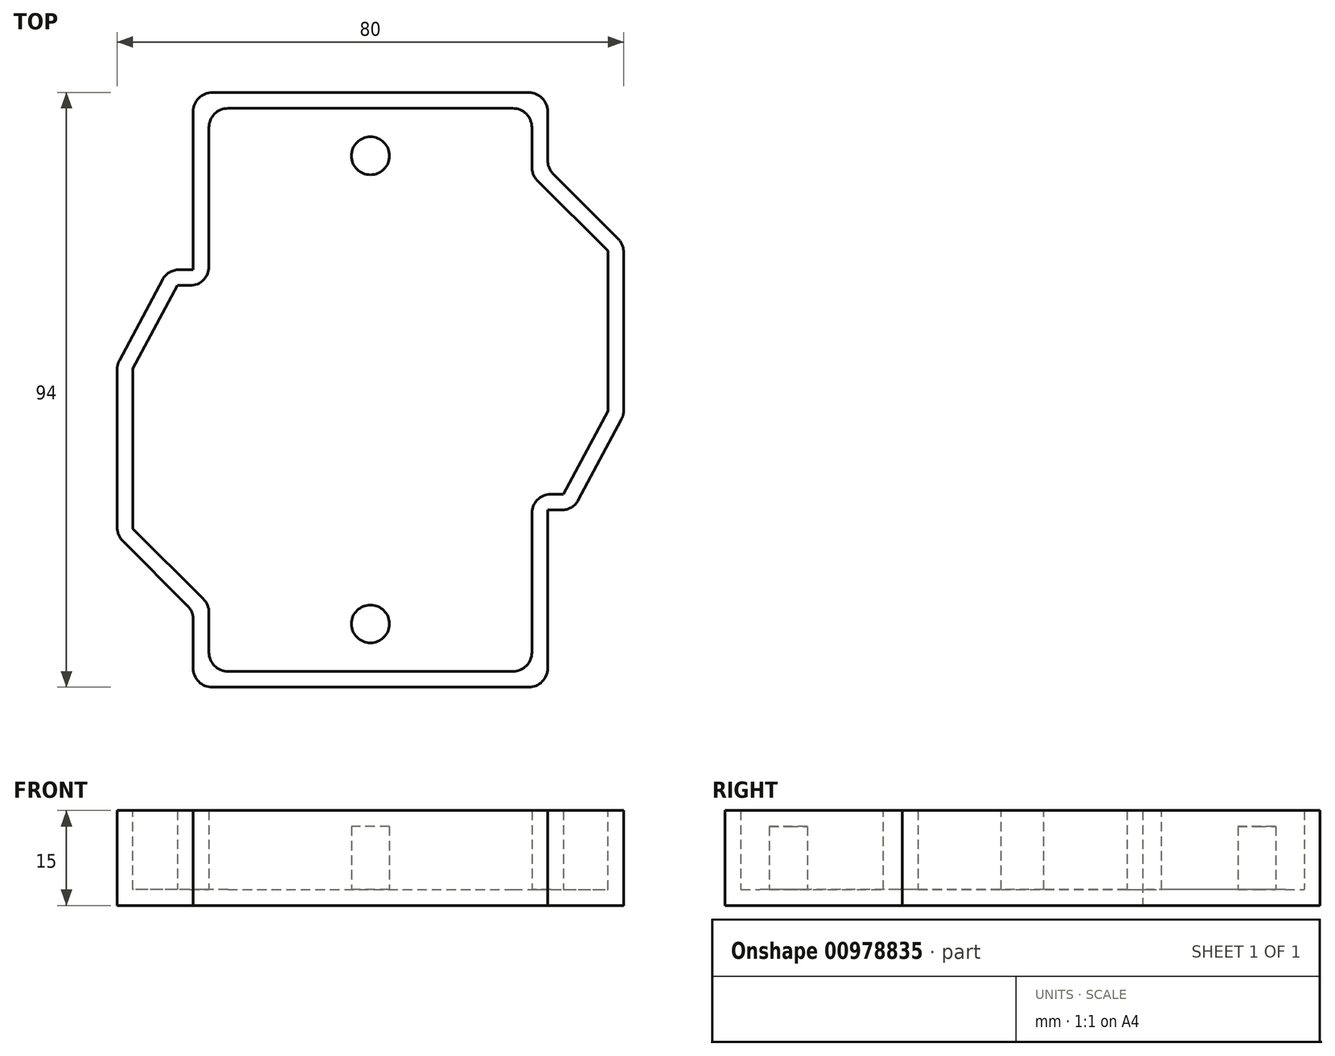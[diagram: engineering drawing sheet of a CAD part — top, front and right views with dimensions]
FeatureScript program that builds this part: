
annotation { "Feature Type Name" : "Feature", "Feature Type Description" : "" }
export const myFeature = defineFeature(function(context is Context, id is Id, definition is map)
    precondition{}
    {
        {
            var Q0;
            Q0=qCreatedBy(makeId("Top.planeOp"),FACE);
            var sketch = newSketch(context, id + "F0", { "sketchPlane" : qUnion([Q0])});
            skLineSegment(sketch, "E0.bottom", {"start": v(-72.44, 119.95) * mm, "end": v(-16.44, 119.95) * mm});
            skLineSegment(sketch, "E0.top", {"start": v(-72.44, 25.95) * mm, "end": v(-16.44, 25.95) * mm});
            skLineSegment(sketch, "E0.left", {"start": v(-72.44, 119.95) * mm, "end": v(-72.44, 25.95) * mm});
            skLineSegment(sketch, "E0.right", {"start": v(-16.44, 119.95) * mm, "end": v(-16.44, 25.95) * mm});
            skLineSegment(sketch, "E1.bottom", {"start": v(-72.44, 91.95) * mm, "end": v(-84.44, 91.95) * mm});
            skLineSegment(sketch, "E1.top", {"start": v(-72.44, 37.95) * mm, "end": v(-84.44, 37.95) * mm});
            skLineSegment(sketch, "E1.left", {"start": v(-72.44, 91.95) * mm, "end": v(-72.44, 37.95) * mm});
            skLineSegment(sketch, "E1.right", {"start": v(-84.44, 91.95) * mm, "end": v(-84.44, 37.95) * mm});
            skLineSegment(sketch, "E2.bottom", {"start": v(-16.44, 53.95) * mm, "end": v(-4.44, 53.95) * mm});
            skLineSegment(sketch, "E2.top", {"start": v(-16.44, 107.95) * mm, "end": v(-4.44, 107.95) * mm});
            skLineSegment(sketch, "E2.left", {"start": v(-16.44, 53.95) * mm, "end": v(-16.44, 107.95) * mm});
            skLineSegment(sketch, "E2.right", {"start": v(-4.44, 53.95) * mm, "end": v(-4.44, 107.95) * mm});
            skSolve(sketch);
        }
        {
            var Q0;
            Q0 = qSketchRegion(id + "F0", true);
            extrude(context, id + "F1", {"entities" : qUnion([Q0]), "depth" : 15 * mm, "offsetDistance" : 25 * mm});
        }
        {
            var Q0;
            Q0=makeQuery(id+"F1.opExtrude","SWEPT_EDGE",EDGE,{"disambiguationData":[OSD([sQuery(id+"F0.wireOp",EDGE,"E1.bottom"),sQuery(id+"F0.wireOp",EDGE,"E1.right")])]});
            var Q1;
            Q1=makeQuery(id+"F1.opExtrude","SWEPT_EDGE",EDGE,{"disambiguationData":[OSD([sQuery(id+"F0.wireOp",EDGE,"E2.bottom"),sQuery(id+"F0.wireOp",EDGE,"E2.right")])]});
            chamfer(context, id + "F2", {"entities" : qUnion([Q0, Q1]), "chamferType" : ChamferType.TWO_OFFSETS, "width1" : 15 * mm, "oppositeDirection" : false, "width2" : 8 * mm, "tangentPropagation" : true});
        }
        {
            var Q0;
            Q0=makeQuery(id+"F1.opExtrude","SWEPT_EDGE",EDGE,{"disambiguationData":[OSD([sQuery(id+"F0.wireOp",EDGE,"E1.top"),sQuery(id+"F0.wireOp",EDGE,"E1.right")])]});
            var Q1;
            Q1=makeQuery(id+"F1.opExtrude","SWEPT_EDGE",EDGE,{"disambiguationData":[OSD([sQuery(id+"F0.wireOp",EDGE,"E2.top"),sQuery(id+"F0.wireOp",EDGE,"E2.right")])]});
            chamfer(context, id + "F3", {"entities" : qUnion([Q0, Q1]), "width" : 12 * mm});
        }
        {
            var Q0;
            Q0=makeQuery(id+"F1.opExtrude","CAP_FACE",FACE,{"disambiguationData":[OSD([sQuery(id+"F0.wireOp",EDGE,"E0.bottom"),sQuery(id+"F0.wireOp",EDGE,"E0.top"),sQuery(id+"F0.wireOp",EDGE,"E0.left"),sQuery(id+"F0.wireOp",EDGE,"E0.right"),sQuery(id+"F0.wireOp",EDGE,"E1.bottom"),sQuery(id+"F0.wireOp",EDGE,"E1.top"),sQuery(id+"F0.wireOp",EDGE,"E1.right"),sQuery(id+"F0.wireOp",EDGE,"E2.bottom"),sQuery(id+"F0.wireOp",EDGE,"E2.top"),sQuery(id+"F0.wireOp",EDGE,"E2.right")])],"isStart":false});
            shell(context, id + "F4", {"entities" : qUnion([Q0]), "thickness" : 2.5 * mm});
        }
        {
            var Q0;
            Q0=makeQuery(id+"F4.opShell","OFFSET_FACE",FACE,{"disambiguationData":[OSD([sQuery(id+"F0.wireOp",EDGE,"E0.bottom"),sQuery(id+"F0.wireOp",EDGE,"E0.top"),sQuery(id+"F0.wireOp",EDGE,"E0.left"),sQuery(id+"F0.wireOp",EDGE,"E0.right"),sQuery(id+"F0.wireOp",EDGE,"E1.bottom"),sQuery(id+"F0.wireOp",EDGE,"E1.top"),sQuery(id+"F0.wireOp",EDGE,"E1.right"),sQuery(id+"F0.wireOp",EDGE,"E2.bottom"),sQuery(id+"F0.wireOp",EDGE,"E2.top"),sQuery(id+"F0.wireOp",EDGE,"E2.right")])]});
            var sketch = newSketch(context, id + "F5", { "sketchPlane" : qUnion([Q0])});
            skCircle(sketch, "E3", {"center": v(-44.44, 109.95) * mm, "radius": 3 * mm});
            skCircle(sketch, "E4", {"center": v(-44.44, 35.95) * mm, "radius": 3 * mm});
            skSolve(sketch);
        }
        {
            var Q0;
            Q0 = qSketchRegion(id + "F5", true);
            extrude(context, id + "F6", {"entities" : qUnion([Q0]), "operationType" : NewBodyOperationType.ADD, "depth" : 10 * mm, "offsetDistance" : 25 * mm});
        }
        {
            var Q0;
            Q0=makeQuery(id+"F1.opExtrude","SWEPT_EDGE",EDGE,{"disambiguationData":[OSD([sQuery(id+"F0.wireOp",EDGE,"E0.bottom"),sQuery(id+"F0.wireOp",EDGE,"E0.left")])]});
            var Q1;
            {var subQ0=sQuery(id+"F0.wireOp",EDGE,"E1.bottom");Q1=makeQuery(id+"F2.opChamfer","BLEND_EDGE",EDGE,{"blendedFrom":[makeQuery(id+"F1.opExtrude","SWEPT_EDGE",EDGE,{"disambiguationData":[OSD([subQ0,sQuery(id+"F0.wireOp",EDGE,"E1.right")])]}),makeQuery(id+"F1.opExtrude","SWEPT_FACE",FACE,{"disambiguationData":[OSD([subQ0])]})],"blendedInto":[makeQuery(id+"F1.opExtrude","SWEPT_FACE",FACE,{"disambiguationData":[OSD([subQ0])]})]});}
            var Q2;
            {var subQ0=sQuery(id+"F0.wireOp",EDGE,"E1.right");Q2=makeQuery(id+"F2.opChamfer","BLEND_EDGE",EDGE,{"blendedFrom":[makeQuery(id+"F1.opExtrude","SWEPT_EDGE",EDGE,{"disambiguationData":[OSD([sQuery(id+"F0.wireOp",EDGE,"E1.bottom"),subQ0])]}),makeQuery(id+"F1.opExtrude","SWEPT_FACE",FACE,{"disambiguationData":[OSD([subQ0])]})],"blendedInto":[makeQuery(id+"F1.opExtrude","SWEPT_FACE",FACE,{"disambiguationData":[OSD([subQ0])]})]});}
            var Q3;
            {var subQ0=sQuery(id+"F0.wireOp",EDGE,"E1.right");Q3=makeQuery(id+"F3.opChamfer","BLEND_EDGE",EDGE,{"blendedFrom":[makeQuery(id+"F1.opExtrude","SWEPT_EDGE",EDGE,{"disambiguationData":[OSD([sQuery(id+"F0.wireOp",EDGE,"E1.top"),subQ0])]}),makeQuery(id+"F1.opExtrude","SWEPT_FACE",FACE,{"disambiguationData":[OSD([subQ0])]})],"blendedInto":[makeQuery(id+"F1.opExtrude","SWEPT_FACE",FACE,{"disambiguationData":[OSD([subQ0])]})]});}
            var Q4;
            {var subQ0=sQuery(id+"F0.wireOp",EDGE,"E0.left");var subQ1=sQuery(id+"F0.wireOp",EDGE,"E1.top");Q4=makeQuery(id+"F3.opChamfer","BLEND_EDGE",EDGE,{"blendedFrom":[makeQuery(id+"F1.opExtrude","SWEPT_EDGE",EDGE,{"disambiguationData":[OSD([subQ1,sQuery(id+"F0.wireOp",EDGE,"E1.right")])]}),makeQuery(id+"F1.opExtrude","SWEPT_FACE",FACE,{"disambiguationData":[OSD([subQ0]),TDD([makeQuery(id+"F0.imprint","IMPRINT",EDGE,{"disambiguationData":[TD([[makeQuery(id+"F0.imprint","INTERSECT",VERTEX,{"derivedFrom":[sQuery(id+"F0.wireOp",EDGE,"E0.top"),subQ0]}),1.0]])],"derivedFrom":subQ0})])]})],"blendedInto":[makeQuery(id+"F1.opExtrude","SWEPT_FACE",FACE,{"disambiguationData":[OSD([subQ0]),TDD([makeQuery(id+"F0.imprint","IMPRINT",EDGE,{"disambiguationData":[TD([[makeQuery(id+"F0.imprint","INTERSECT",VERTEX,{"derivedFrom":[sQuery(id+"F0.wireOp",EDGE,"E0.top"),subQ0]}),1.0]])],"derivedFrom":subQ0})])]})]});}
            var Q5;
            Q5=makeQuery(id+"F1.opExtrude","SWEPT_EDGE",EDGE,{"disambiguationData":[OSD([sQuery(id+"F0.wireOp",EDGE,"E0.top"),sQuery(id+"F0.wireOp",EDGE,"E0.left")])]});
            var Q6;
            Q6=makeQuery(id+"F1.opExtrude","SWEPT_EDGE",EDGE,{"disambiguationData":[OSD([sQuery(id+"F0.wireOp",EDGE,"E0.top"),sQuery(id+"F0.wireOp",EDGE,"E0.right")])]});
            var Q7;
            {var subQ0=sQuery(id+"F0.wireOp",EDGE,"E2.bottom");Q7=makeQuery(id+"F2.opChamfer","BLEND_EDGE",EDGE,{"blendedFrom":[makeQuery(id+"F1.opExtrude","SWEPT_EDGE",EDGE,{"disambiguationData":[OSD([subQ0,sQuery(id+"F0.wireOp",EDGE,"E2.right")])]}),makeQuery(id+"F1.opExtrude","SWEPT_FACE",FACE,{"disambiguationData":[OSD([subQ0])]})],"blendedInto":[makeQuery(id+"F1.opExtrude","SWEPT_FACE",FACE,{"disambiguationData":[OSD([subQ0])]})]});}
            var Q8;
            {var subQ0=sQuery(id+"F0.wireOp",EDGE,"E2.right");Q8=makeQuery(id+"F2.opChamfer","BLEND_EDGE",EDGE,{"blendedFrom":[makeQuery(id+"F1.opExtrude","SWEPT_EDGE",EDGE,{"disambiguationData":[OSD([sQuery(id+"F0.wireOp",EDGE,"E2.bottom"),subQ0])]}),makeQuery(id+"F1.opExtrude","SWEPT_FACE",FACE,{"disambiguationData":[OSD([subQ0])]})],"blendedInto":[makeQuery(id+"F1.opExtrude","SWEPT_FACE",FACE,{"disambiguationData":[OSD([subQ0])]})]});}
            var Q9;
            {var subQ0=sQuery(id+"F0.wireOp",EDGE,"E2.right");Q9=makeQuery(id+"F3.opChamfer","BLEND_EDGE",EDGE,{"blendedFrom":[makeQuery(id+"F1.opExtrude","SWEPT_EDGE",EDGE,{"disambiguationData":[OSD([sQuery(id+"F0.wireOp",EDGE,"E2.top"),subQ0])]}),makeQuery(id+"F1.opExtrude","SWEPT_FACE",FACE,{"disambiguationData":[OSD([subQ0])]})],"blendedInto":[makeQuery(id+"F1.opExtrude","SWEPT_FACE",FACE,{"disambiguationData":[OSD([subQ0])]})]});}
            var Q10;
            {var subQ0=sQuery(id+"F0.wireOp",EDGE,"E0.right");var subQ1=sQuery(id+"F0.wireOp",EDGE,"E2.top");Q10=makeQuery(id+"F3.opChamfer","BLEND_EDGE",EDGE,{"blendedFrom":[makeQuery(id+"F1.opExtrude","SWEPT_EDGE",EDGE,{"disambiguationData":[OSD([subQ1,sQuery(id+"F0.wireOp",EDGE,"E2.right")])]}),makeQuery(id+"F1.opExtrude","SWEPT_FACE",FACE,{"disambiguationData":[OSD([subQ0]),TDD([makeQuery(id+"F0.imprint","IMPRINT",EDGE,{"disambiguationData":[TD([[makeQuery(id+"F0.imprint","INTERSECT",VERTEX,{"derivedFrom":[sQuery(id+"F0.wireOp",EDGE,"E0.bottom"),subQ0]}),-1.0]])],"derivedFrom":subQ0})])]})],"blendedInto":[makeQuery(id+"F1.opExtrude","SWEPT_FACE",FACE,{"disambiguationData":[OSD([subQ0]),TDD([makeQuery(id+"F0.imprint","IMPRINT",EDGE,{"disambiguationData":[TD([[makeQuery(id+"F0.imprint","INTERSECT",VERTEX,{"derivedFrom":[sQuery(id+"F0.wireOp",EDGE,"E0.bottom"),subQ0]}),-1.0]])],"derivedFrom":subQ0})])]})]});}
            var Q11;
            Q11=makeQuery(id+"F1.opExtrude","SWEPT_EDGE",EDGE,{"disambiguationData":[OSD([sQuery(id+"F0.wireOp",EDGE,"E0.bottom"),sQuery(id+"F0.wireOp",EDGE,"E0.right")])]});
            var Q12;
            Q12=makeQuery(id+"F4.opShell","OFFSET_EDGE",EDGE,{"disambiguationData":[OSD([sQuery(id+"F0.wireOp",EDGE,"E0.bottom"),sQuery(id+"F0.wireOp",EDGE,"E0.left")])]});
            var Q13;
            Q13=makeQuery(id+"F4.opShell","OFFSET_EDGE",EDGE,{"disambiguationData":[OSD([sQuery(id+"F0.wireOp",EDGE,"E0.left"),sQuery(id+"F0.wireOp",EDGE,"E1.bottom"),sQuery(id+"F0.wireOp",EDGE,"E1.left")])]});
            var Q14;
            Q14=makeQuery(id+"F4.opShell","OFFSET_EDGE",EDGE,{"disambiguationData":[OSD([sQuery(id+"F0.wireOp",EDGE,"E0.bottom"),sQuery(id+"F0.wireOp",EDGE,"E0.right")])]});
            var Q15;
            Q15=makeQuery(id+"F4.opShell","OFFSET_EDGE",EDGE,{"disambiguationData":[OSD([sQuery(id+"F0.wireOp",EDGE,"E0.right"),sQuery(id+"F0.wireOp",EDGE,"E2.top"),sQuery(id+"F0.wireOp",EDGE,"E2.right")])]});
            var Q16;
            Q16=makeQuery(id+"F4.opShell","OFFSET_EDGE",EDGE,{"disambiguationData":[OSD([sQuery(id+"F0.wireOp",EDGE,"E0.left"),sQuery(id+"F0.wireOp",EDGE,"E1.top"),sQuery(id+"F0.wireOp",EDGE,"E1.right")])]});
            var Q17;
            Q17=makeQuery(id+"F4.opShell","OFFSET_EDGE",EDGE,{"disambiguationData":[OSD([sQuery(id+"F0.wireOp",EDGE,"E0.top"),sQuery(id+"F0.wireOp",EDGE,"E0.left")])]});
            var Q18;
            Q18=makeQuery(id+"F4.opShell","OFFSET_EDGE",EDGE,{"disambiguationData":[OSD([sQuery(id+"F0.wireOp",EDGE,"E0.right"),sQuery(id+"F0.wireOp",EDGE,"E2.bottom"),sQuery(id+"F0.wireOp",EDGE,"E2.left")])]});
            var Q19;
            Q19=makeQuery(id+"F4.opShell","OFFSET_EDGE",EDGE,{"disambiguationData":[OSD([sQuery(id+"F0.wireOp",EDGE,"E0.top"),sQuery(id+"F0.wireOp",EDGE,"E0.right")])]});
            fillet(context, id + "F7", {"entities" : qUnion([Q0, Q1, Q2, Q3, Q4, Q5, Q6, Q7, Q8, Q9, Q10, Q11, Q12, Q13, Q14, Q15, Q16, Q17, Q18, Q19]), "radius" : 3 * mm, "tangentPropagation" : true, "allowEdgeOverflow" : false});
        }
    });
